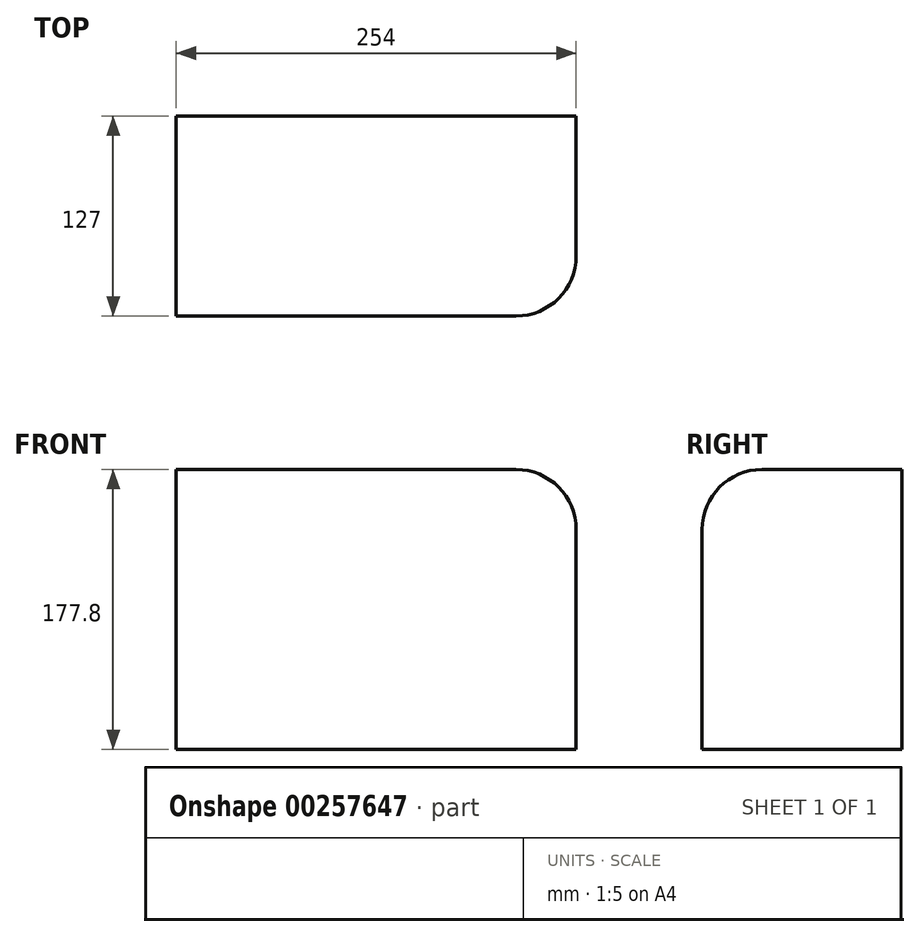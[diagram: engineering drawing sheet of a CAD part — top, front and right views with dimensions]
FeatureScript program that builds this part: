
annotation { "Feature Type Name" : "Feature", "Feature Type Description" : "" }
export const myFeature = defineFeature(function(context is Context, id is Id, definition is map)
    precondition{}
    {
        {
            var Q0;
            Q0=qCreatedBy(makeId("Front.planeOp"),FACE);
            var sketch = newSketch(context, id + "F0", { "sketchPlane" : qUnion([Q0])});
            skLineSegment(sketch, "E0.bottom", {"start": v(-118.78, 87.69) * mm, "end": v(135.22, 87.69) * mm});
            skLineSegment(sketch, "E0.top", {"start": v(-118.78, -90.11) * mm, "end": v(135.22, -90.11) * mm});
            skLineSegment(sketch, "E0.left", {"start": v(-118.78, 87.69) * mm, "end": v(-118.78, -90.11) * mm});
            skLineSegment(sketch, "E0.right", {"start": v(135.22, 87.69) * mm, "end": v(135.22, -90.11) * mm});
            skSolve(sketch);
        }
        {
            var Q0;
            Q0=makeQuery(id+"F0.imprint","IMPRINT",FACE,{"disambiguationData":[TD([[makeQuery(id+"F0.imprint","IMPRINT",EDGE,{"derivedFrom":sQuery(id+"F0.wireOp",EDGE,"E0.bottom")}),-1.0]])]});
            extrude(context, id + "F1", {"entities" : qUnion([Q0]), "depth" : 127 * mm});
        }
        {
            var Q0;
            Q0=makeQuery(id+"F1.opExtrude","CAP_EDGE",EDGE,{"disambiguationData":[OSD([sQuery(id+"F0.wireOp",EDGE,"E0.bottom")])],"isStart":false});
            var Q1;
            Q1=makeQuery(id+"F1.opExtrude","SWEPT_EDGE",EDGE,{"disambiguationData":[OSD([sQuery(id+"F0.wireOp",EDGE,"E0.bottom"),sQuery(id+"F0.wireOp",EDGE,"E0.right")])]});
            var Q2;
            Q2=makeQuery(id+"F1.opExtrude","CAP_EDGE",EDGE,{"disambiguationData":[OSD([sQuery(id+"F0.wireOp",EDGE,"E0.right")])],"isStart":false});
            fillet(context, id + "F2", {"entities" : qUnion([Q0, Q1, Q2]), "radius" : 38.1 * mm, "tangentPropagation" : true, "allowEdgeOverflow" : false});
        }
    });
